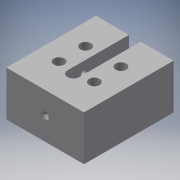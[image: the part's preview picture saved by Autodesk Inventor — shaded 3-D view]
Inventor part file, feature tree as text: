
AUTODESK INVENTOR PART (.ipt)
format: ipt  version: 2016 (Build 200138000, 138)  size: 180,224 bytes
history: native  units: mm (DEFAULTED — no unit token found)
features: extrude x5, sketch x5, hole x2, fillet x1
ambient origin geometry x8: Origin, YZ Plane, XZ Plane, XY Plane, X Axis, Y Axis, Z Axis, Center Point
bodies: Solid1 (feature_tree)
feature tree (13):
  extrude  "Extrusion1"  Depth=44.0mm
  hole  "Hole1"  [1 undecoded]
  extrude  "Extrusion2"  Depth=6.0mm
  hole  "Hole2"  [1 undecoded]
  extrude  "Extrusion4"  Depth=3.175mm
  extrude  "Extrusion5"  Depth=3.175mm TaperAngle=0.0deg
  extrude  "Extrusion6"  Depth=3.175mm
  fillet  "Fillet1"  Radius=6.35mm
  sketch  "Sketch2"  dims[d0=50.8mm d1=44.0mm]
  sketch  "Sketch3"  dims[d2=25.4mm d3=0.0mm]
  sketch  "Sketch4"  dims[d4=4.134mm d5=10.0mm d6=4.0mm d7=2.0mm d8=90.0deg d9=12.7mm d10=20.594885mm d11=20.0mm]
  sketch  "Sketch5"  dims[d12=15.0mm d13=6.0mm]
  sketch  "Sketch9"  dims[d14=6.0mm d15=6.0mm d16=6.0mm d17=5.0mm d18=0.0mm d19=3.5mm d20=6.0mm d21=4.0mm d22=2.0mm d23=90.0deg d24=8.0mm d25=20.594885mm d31=3.5mm d32=6.35mm d33=25.4mm d34=22.0mm d35=0.0mm d36=6.604mm d37=22.0mm d38=19.05mm d39=38.1mm d40=0.0mm d41=3.5mm d42=7.9375mm d43=6.0mm d44=6.0mm d45=3.0mm d46=0.0mm d47=3.175mm]
note: 2 required parameter values undecoded (feature->parameter linkage not recoverable at this tier; creation-order binding heuristic only, values carry confidence <= 0.55)
